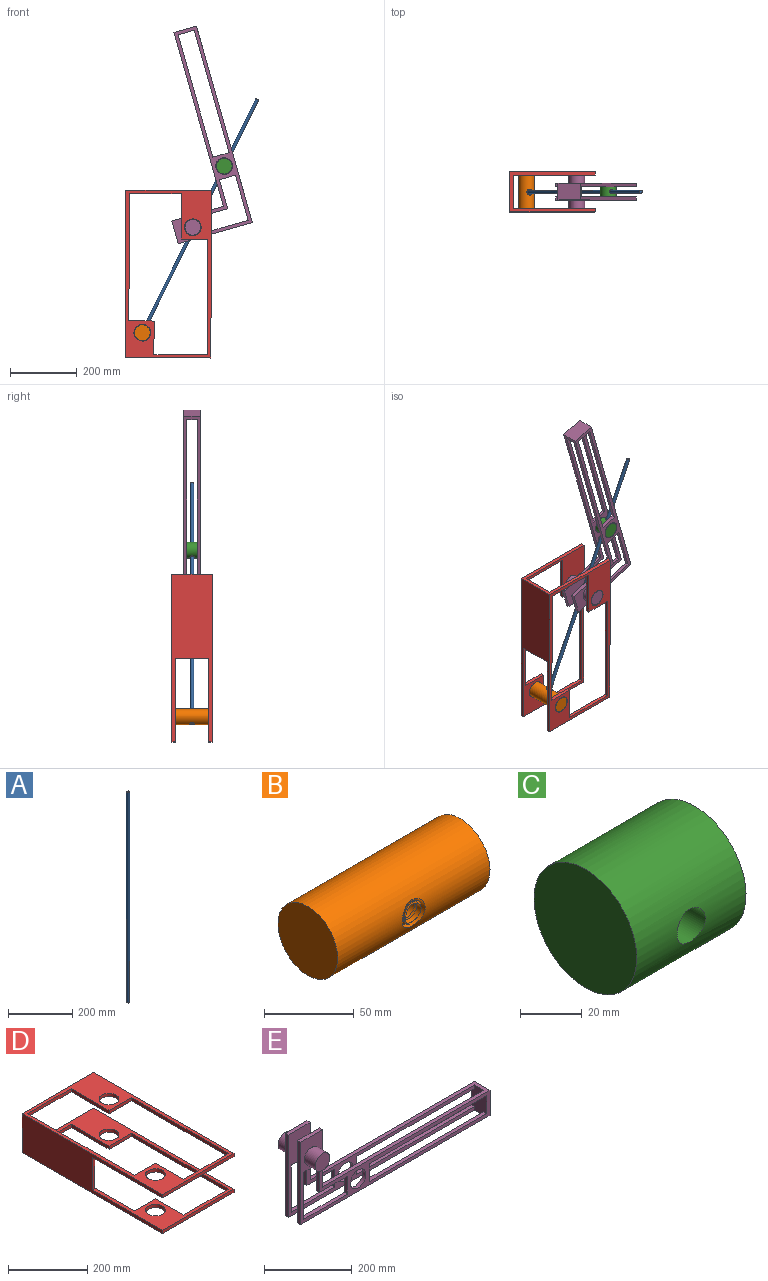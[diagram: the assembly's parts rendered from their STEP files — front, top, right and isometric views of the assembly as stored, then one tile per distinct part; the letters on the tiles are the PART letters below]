
ASSEMBLY  parts=5 mates=5
PART A: 3 faces, bbox 10x10x800 mm
  f0: cylinder r=5mm len=800mm, axis (0,0,-1), area 25132.7mm2, adj f1,f2
  f1: plane 10x10mm, normal (0,0,1), area 78.5mm2, adj f0
  f2: plane 10x10mm, normal (0,0,-1), area 78.5mm2, adj f0
PART B: 18 faces, bbox 120x48.7x47 mm
  f0: cylinder r=23.5mm len=120mm, axis (-1,0,0), area 17326.1mm2, adj f1,f11,f12,f13
  f1: cylinder r=6.5mm len=13mm, axis (0,1,0), area 373.7mm2, adj f0,f2,f14,f15,f16
  f2: cylinder r=6.5mm len=13mm, axis (0,1,0), area 132.8mm2, adj f1,f3,f15,f16
  f3: cylinder r=6.5mm len=13mm, axis (0,1,0), area 132.8mm2, adj f2,f4,f15,f16
  f4: cylinder r=6.5mm len=13mm, axis (0,1,0), area 132.8mm2, adj f3,f5,f15,f16
  f5: cylinder r=6.5mm len=13mm, axis (0,1,0), area 132.8mm2, adj f4,f6,f15,f16
  f6: cylinder r=6.5mm len=13mm, axis (0,1,0), area 132.8mm2, adj f5,f7,f15,f16
  f7: cylinder r=6.5mm len=13mm, axis (0,1,0), area 132.8mm2, adj f6,f8,f15,f16
  f8: cylinder r=6.5mm len=13mm, axis (0,1,0), area 129.1mm2, adj f7,f9,f10,f15,f16
  f9: cylinder r=6.5mm len=12.36mm, axis (0,1,0), area 17.2mm2, adj f8,f10,f16
  f10: cylinder r=23.5mm len=13.46mm, axis (-1,0,0), area 23.3mm2, adj f8,f9,f15,f16
  f11: plane 47x47mm, normal (1,0,0), area 1734.9mm2, adj f0
  f12: plane 47x47mm, normal (-1,0,0), area 1734.9mm2, adj f0
  f13: cylinder r=8.98mm len=41.22mm, axis (0,1,0), area 2185.7mm2, adj f0,f14,f17
  f14: plane 6.01x3.66mm, normal (0.6,0,0.8), area 18.2mm2, adj f1,f13,f15,f16,f17
  f15: bspline ~42.41x15.26mm, area 691mm2, adj f1,f2,f3,f4,f5,f6,f7,f8
  f16: bspline ~41.67x17.79mm, area 766.8mm2, adj f1,f2,f3,f4,f5,f6,f7,f8
  f17: bspline ~20.58x19.11mm, area 77mm2, adj f13,f14,f15
PART C: 4 faces, bbox 50x47x47 mm
  f0: cylinder r=23.5mm len=50mm, axis (1,0,0), area 7114.4mm2, adj f1,f2,f3
  f1: plane 47x47mm, normal (-1,0,0), area 1734.9mm2, adj f0
  f2: cylinder r=6.5mm len=47mm, axis (0,1,0), area 1882.3mm2, adj f0
  f3: plane 47x47mm, normal (1,0,0), area 1734.9mm2, adj f0
PART D: 32 faces, bbox 255x500x120 mm
  f0: plane 255x10mm, normal (0,-1,0), area 2550mm2, adj f1,f3,f6,f9
  f1: plane 500x10mm, normal (1,0,0), area 5000mm2, adj f0,f2,f6,f9
  f2: plane 255x120mm, normal (0,1,0), area 6080mm2, adj f1,f3,f5,f6,f7,f8,f9,f10
  f3: plane 500x120mm, normal (-1,0,0), area 35000mm2, adj f0,f2,f4,f6,f7,f8,f9,f15
  f4: plane 255x10mm, normal (0,-1,0), area 2550mm2, adj f3,f5,f7,f8
  f5: plane 500x10mm, normal (1,0,0), area 5000mm2, adj f2,f4,f7,f8
  f6: plane 500x255mm, normal (0,0,1), area 29073mm2, adj f0,f1,f2,f3,f11,f12,f16,f17
  f7: plane 500x255mm, normal (0,0,-1), area 29073mm2, adj f2,f3,f4,f5,f13,f14,f24,f25
  f8: plane 500x255mm, normal (0,0,1), area 26623mm2, adj f2,f3,f4,f5,f10,f13,f14,f15
  f9: plane 500x255mm, normal (0,0,-1), area 26623mm2, adj f0,f1,f2,f3,f10,f11,f12,f15
  f10: plane 250x100mm, normal (1,0,0), area 25000mm2, adj f2,f8,f9,f15
  f11: cylinder r=25mm len=50mm, axis (0,0,1), area 1570.8mm2, adj f6,f9
  f12: cylinder r=25mm len=50mm, axis (0,0,1), area 1570.8mm2, adj f6,f9
  f13: cylinder r=25mm len=50mm, axis (0,0,1), area 1570.8mm2, adj f7,f8
  f14: cylinder r=25mm len=50mm, axis (0,0,1), area 1570.8mm2, adj f7,f8
  f15: plane 100x9.8mm, normal (0,-1,0), area 980mm2, adj f3,f8,f9,f10
  f16: plane 155x10mm, normal (0,-1,0), area 1550mm2, adj f6,f9,f17,f23
  f17: plane 135x10mm, normal (-1,0,0), area 1350mm2, adj f6,f9,f16,f18
  f18: plane 80x10mm, normal (0,-1,0), area 800mm2, adj f6,f9,f17,f19
  f19: plane 345x10mm, normal (-1,0,0), area 3450mm2, adj f6,f9,f18,f20
  f20: plane 160x10mm, normal (0,1,0), area 1600mm2, adj f6,f9,f19,f21
  f21: plane 100x10mm, normal (1,0,0), area 1000mm2, adj f6,f9,f20,f22
  f22: plane 75x10mm, normal (0,1,0), area 750mm2, adj f6,f9,f21,f23
  f23: plane 380x10mm, normal (1,0,0), area 3800mm2, adj f6,f9,f16,f22
  f24: plane 380x10mm, normal (1,0,0), area 3800mm2, adj f7,f8,f25,f31
  f25: plane 75x10mm, normal (0,1,0), area 750mm2, adj f7,f8,f24,f26
  f26: plane 100x10mm, normal (1,0,0), area 1000mm2, adj f7,f8,f25,f27
  f27: plane 160x10mm, normal (0,1,0), area 1600mm2, adj f7,f8,f26,f28
  f28: plane 345x10mm, normal (-1,0,0), area 3450mm2, adj f7,f8,f27,f29
  f29: plane 80x10mm, normal (0,-1,0), area 800mm2, adj f7,f8,f28,f30
  f30: plane 135x10mm, normal (-1,0,0), area 1350mm2, adj f7,f8,f29,f31
  f31: plane 155x10mm, normal (0,-1,0), area 1550mm2, adj f7,f8,f24,f30
PART E: 38 faces, bbox 610x120x230 mm
  f0: plane 610x230mm, normal (0,-1,0), area 20126.6mm2, adj f4,f7,f9,f10,f11,f12,f13,f17
  f1: plane 610x230mm, normal (0,1,0), area 20126.6mm2, adj f5,f6,f7,f8,f9,f10,f15,f17
  f2: plane 600x230mm, normal (0,-1,0), area 21161.5mm2, adj f5,f6,f7,f8,f9,f17,f19,f29
  f3: plane 600x230mm, normal (0,1,0), area 21161.5mm2, adj f4,f7,f9,f11,f12,f17,f18,f20
  f4: plane 230x10mm, normal (-1,0,0), area 2300mm2, adj f0,f3,f9,f12
  f5: plane 70x10mm, normal (0,0,1), area 700mm2, adj f1,f2,f6,f8
  f6: plane 230x10mm, normal (-1,0,0), area 2300mm2, adj f1,f2,f5,f9
  f7: plane 540x50mm, normal (0,0,1), area 11100mm2, adj f0,f1,f2,f3,f8,f10,f11,f17
  f8: plane 160x10mm, normal (1,0,0), area 1600mm2, adj f1,f2,f5,f7
  f9: plane 610x50mm, normal (0,0,-1), area 12500mm2, adj f0,f1,f2,f3,f4,f6,f10,f17
  f10: plane 70x50mm, normal (1,0,0), area 3500mm2, adj f0,f1,f7,f9
  f11: plane 160x10mm, normal (1,0,0), area 1600mm2, adj f0,f3,f7,f12
  f12: plane 70x10mm, normal (0,0,1), area 700mm2, adj f0,f3,f4,f11
  f13: cylinder r=23.5mm len=47mm, axis (0,1,0), area 5167.9mm2, adj f0,f14
  f14: plane 47x47mm, normal (0,-1,0), area 1734.9mm2, adj f13
  f15: cylinder r=23.5mm len=47mm, axis (0,-1,0), area 5167.9mm2, adj f1,f16
  f16: plane 47x47mm, normal (0,1,0), area 1734.9mm2, adj f15
  f17: plane 70x50mm, normal (-1,0,0), area 3100mm2, adj f0,f1,f2,f3,f7,f9,f26,f28
  f18: cylinder r=25mm len=50mm, axis (0,-1,0), area 1570.8mm2, adj f0,f3
  f19: cylinder r=25mm len=50mm, axis (0,-1,0), area 1570.8mm2, adj f1,f2
  f20: plane 50x10mm, normal (-1,0,0), area 500mm2, adj f0,f3,f21,f25
  f21: plane 140x10mm, normal (0,0,1), area 1400mm2, adj f0,f3,f20,f22
  f22: plane 131.5x10mm, normal (1,0,0), area 1315mm2, adj f0,f3,f21,f23
  f23: plane 50x10mm, normal (0,0,-1), area 500mm2, adj f0,f3,f22,f24
  f24: plane 81.5x10mm, normal (-1,0,0), area 815mm2, adj f0,f3,f23,f25
  f25: plane 90x10mm, normal (0,0,-1), area 900mm2, adj f0,f3,f20,f24
  f26: plane 380x10mm, normal (0,0,1), area 3800mm2, adj f0,f3,f17,f27
  f27: plane 50x10mm, normal (1,0,0), area 500mm2, adj f0,f3,f26,f28
  f28: plane 380x10mm, normal (0,0,-1), area 3800mm2, adj f0,f3,f17,f27
  f29: plane 90x10mm, normal (0,0,-1), area 900mm2, adj f1,f2,f30,f34
  f30: plane 81.5x10mm, normal (-1,0,0), area 815mm2, adj f1,f2,f29,f31
  f31: plane 50x10mm, normal (0,0,-1), area 500mm2, adj f1,f2,f30,f32
  f32: plane 131.5x10mm, normal (1,0,0), area 1315mm2, adj f1,f2,f31,f33
  f33: plane 140x10mm, normal (0,0,1), area 1400mm2, adj f1,f2,f32,f34
  f34: plane 50x10mm, normal (-1,0,0), area 500mm2, adj f1,f2,f29,f33
  f35: plane 380x10mm, normal (0,0,-1), area 3800mm2, adj f1,f2,f17,f36
  f36: plane 50x10mm, normal (1,0,0), area 500mm2, adj f1,f2,f35,f37
  f37: plane 380x10mm, normal (0,0,1), area 3800mm2, adj f1,f2,f17,f36
PLACE A rot(axis=(0,1,0),26.2deg) t=(-77.01,66.65,4.2)mm
PLACE B rot(axis=(-0.47,-0.47,0.75),106.2deg) t=(-74.59,16.65,-104.2)mm
PLACE C rot(axis=(-0.47,-0.47,0.75),106.2deg) t=(165.61,41.65,361.64)mm
PLACE D rot(axis=(1,0,0),90deg) t=(-116.7,126.65,-49.32)mm fixed
PLACE E rot(axis=(0,-1,0),105.9deg) t=(262.19,91.65,354.34)mm
MATE revolute E.f13 <-> D.f11  axis (0,-1,0) through (84.29,6.65,340.17)mm
MATE slider A.f0 <-> C.f2  axis (-0.44,0,-0.9) through (99.49,66.65,363.15)mm
MATE revolute B.f0 <-> D.f12  axis (0,-1,0) through (-66.51,6.65,25.55)mm
MATE revolute C.f0 <-> E.f18  axis (0,-1,0) through (177.95,41.65,522.73)mm
MATE revolute A.f0 <-> B.f1  axis (-0.44,0,-0.9) through (-77.01,66.65,4.2)mm
